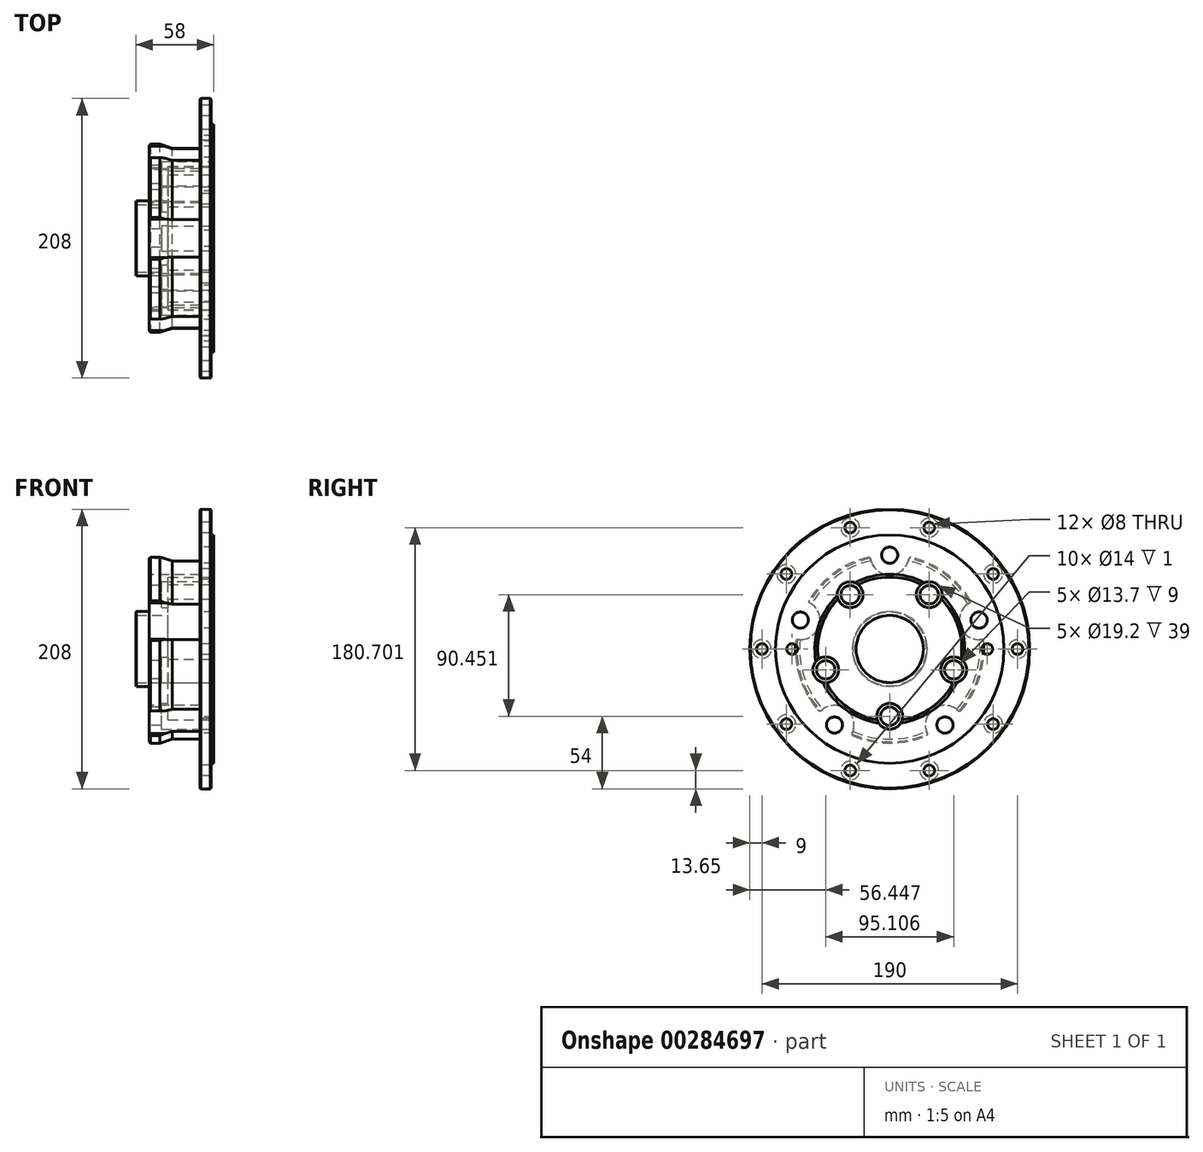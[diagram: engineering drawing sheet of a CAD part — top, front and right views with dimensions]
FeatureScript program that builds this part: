
annotation { "Feature Type Name" : "Feature", "Feature Type Description" : "" }
export const myFeature = defineFeature(function(context is Context, id is Id, definition is map)
    precondition{}
    {
        {
            var Q0;
            Q0=qCreatedBy(makeId("Front.planeOp"),FACE);
            var sketch = newSketch(context, id + "F0", { "sketchPlane" : qUnion([Q0])});
            skLineSegment(sketch, "E0", {"start": v(0, 0) * mm, "end": v(-58, 0) * mm});
            skLineSegment(sketch, "E1", {"start": v(0, 53.5) * mm, "end": v(0, 84.9) * mm});
            skLineSegment(sketch, "E2", {"start": v(0, 84.9) * mm, "end": v(-2.2, 84.9) * mm});
            skPoint(sketch, "E3", {"position": v(-2.2, 104) * mm});
            skLineSegment(sketch, "E4", {"start": v(-2.2, 84.9) * mm, "end": v(-2.2, 104) * mm});
            skLineSegment(sketch, "E5", {"start": v(-2.2, 104) * mm, "end": v(-10.2, 104) * mm});
            skPoint(sketch, "E6", {"position": v(-10.2, 67) * mm});
            skLineSegment(sketch, "E7", {"start": v(-10.2, 104) * mm, "end": v(-10.2, 67) * mm});
            skLineSegment(sketch, "E8", {"start": v(-10.2, 67) * mm, "end": v(-31, 67) * mm});
            skLineSegment(sketch, "E9", {"start": v(-31, 67) * mm, "end": v(-34, 67) * mm});
            skPoint(sketch, "E10", {"position": v(-48, 70) * mm});
            skLineSegment(sketch, "E11", {"start": v(-48, 70) * mm, "end": v(-48, 25) * mm});
            skPoint(sketch, "E12", {"position": v(-58, 27.85) * mm});
            skLineSegment(sketch, "E13", {"start": v(-58, 27.85) * mm, "end": v(-48, 27.85) * mm});
            skPoint(sketch, "E14", {"position": v(-58, 25) * mm});
            skLineSegment(sketch, "E15", {"start": v(-58, 25) * mm, "end": v(-48, 25) * mm});
            skLineSegment(sketch, "E16", {"start": v(-58, 27.85) * mm, "end": v(-58, 25) * mm});
            skPoint(sketch, "E17", {"position": v(0, 53.5) * mm});
            skLineSegment(sketch, "E18", {"start": v(0, 53.5) * mm, "end": v(-34, 53.5) * mm});
            skLineSegment(sketch, "E19", {"start": v(-34, 67) * mm, "end": v(-34, 0) * mm});
            skLineSegment(sketch, "E20", {"start": v(-34, 53.5) * mm, "end": v(-34, 25) * mm});
            skLineSegment(sketch, "E21", {"start": v(-48, 25) * mm, "end": v(-34, 25) * mm});
            skPoint(sketch, "E22.orphan", {"position": v(-34, 0) * mm});
            skPoint(sketch, "E23.orphan", {"position": v(-48, 0) * mm});
            skLineSegment(sketch, "E24", {"start": v(-48, 70) * mm, "end": v(-40, 70) * mm});
            skLineSegment(sketch, "E25", {"start": v(-40, 70) * mm, "end": v(-31, 67) * mm});
            skSolve(sketch);
        }
        {
            var Q0;
            Q0=qSketchRegion(id+"F0",true);
            var Q1;
            Q1=sQuery(id+"F0.wireOp",EDGE,"E0");
            revolve(context, id + "F1", {"entities" : qUnion([Q0]), "axis" : qUnion([Q1]), "revolveType" : RevolveType.FULL});
        }
        {
            var Q0;
            Q0=makeQuery(id+"F1.opRevolve","SWEPT_FACE",FACE,{"disambiguationData":[OSD([sQuery(id+"F0.wireOp",EDGE,"E11")])]});
            var sketch = newSketch(context, id + "F2", { "sketchPlane" : qUnion([Q0])});
            skPoint(sketch, "E26", {"position": v(0, 0) * mm});
            skCircle(sketch, "E27", {"center": v(0, 0) * mm, "radius": 69.85 * mm, "construction": true});
            skLineSegment(sketch, "E28", {"start": v(0, 0) * mm, "end": v(0, 69.85) * mm});
            skCircle(sketch, "E29", {"center": v(0, 69.85) * mm, "radius": 6 * mm});
            skCircle(sketch, "E30.1.0", {"center": v(-66.43, 21.58) * mm, "radius": 6 * mm});
            skCircle(sketch, "E30.2.0", {"center": v(-41.06, -56.5) * mm, "radius": 6 * mm});
            skCircle(sketch, "E30.3.0", {"center": v(41.06, -56.5) * mm, "radius": 6 * mm});
            skCircle(sketch, "E30.4.0", {"center": v(66.43, 21.58) * mm, "radius": 6 * mm});
            skSolve(sketch);
        }
        {
            var Q0;
            {var subQ0=sQuery(id+"F2.wireOp",EDGE,"9778c2bb-2c79-4bee-9a48-f8a60644cc8f.1.0");var subQ1=makeQuery(id+"F1.opRevolve","SWEPT_EDGE",EDGE,{"disambiguationData":[OSD([sQuery(id+"F0.wireOp",EDGE,"E11"),sQuery(id+"F0.wireOp",EDGE,"E24")])]});var subQ2=makeQuery(id+"F2.imprint","INTERSECT",VERTEX,{"disambiguationData":[OD(0.0)],"derivedFrom":[subQ1,subQ0]});Q0=makeQuery(id+"F2.imprint","IMPRINT",FACE,{"disambiguationData":[TD([[makeQuery(id+"F2.imprint","IMPRINT",EDGE,{"disambiguationData":[TD([[subQ2,1.0]])],"derivedFrom":subQ0}),1.0]])]});}
            var Q1;
            {var subQ0=sQuery(id+"F2.wireOp",EDGE,"9778c2bb-2c79-4bee-9a48-f8a60644cc8f.1.0");var subQ1=makeQuery(id+"F1.opRevolve","SWEPT_EDGE",EDGE,{"disambiguationData":[OSD([sQuery(id+"F0.wireOp",EDGE,"E11"),sQuery(id+"F0.wireOp",EDGE,"E24")])]});var subQ2=makeQuery(id+"F2.imprint","INTERSECT",VERTEX,{"disambiguationData":[OD(0.0)],"derivedFrom":[subQ1,subQ0]});Q1=makeQuery(id+"F2.imprint","IMPRINT",FACE,{"disambiguationData":[TD([[makeQuery(id+"F2.imprint","IMPRINT",EDGE,{"disambiguationData":[TD([[subQ2,-1.0]])],"derivedFrom":subQ0}),1.0]])]});}
            var Q2;
            {var subQ0=sQuery(id+"F2.wireOp",EDGE,"E29");var subQ1=makeQuery(id+"F1.opRevolve","SWEPT_EDGE",EDGE,{"disambiguationData":[OSD([sQuery(id+"F0.wireOp",EDGE,"E11"),sQuery(id+"F0.wireOp",EDGE,"E24")])]});var subQ2=makeQuery(id+"F2.imprint","INTERSECT",VERTEX,{"disambiguationData":[OD(0.0)],"derivedFrom":[subQ1,subQ0]});Q2=makeQuery(id+"F2.imprint","IMPRINT",FACE,{"disambiguationData":[TD([[makeQuery(id+"F2.imprint","IMPRINT",EDGE,{"disambiguationData":[TD([[subQ2,1.0]])],"derivedFrom":subQ0}),1.0]])]});}
            var Q3;
            {var subQ0=sQuery(id+"F2.wireOp",EDGE,"E29");var subQ1=makeQuery(id+"F2.imprint","IMPRINT",VERTEX,{"derivedFrom":subQ0});Q3=makeQuery(id+"F2.imprint","IMPRINT",FACE,{"disambiguationData":[TD([[makeQuery(id+"F2.imprint","IMPRINT",EDGE,{"disambiguationData":[TD([[subQ1,1.0]])],"derivedFrom":subQ0}),1.0]])]});}
            var Q4;
            {var subQ0=sQuery(id+"F2.wireOp",EDGE,"9778c2bb-2c79-4bee-9a48-f8a60644cc8f.4.0");var subQ1=makeQuery(id+"F1.opRevolve","SWEPT_EDGE",EDGE,{"disambiguationData":[OSD([sQuery(id+"F0.wireOp",EDGE,"E11"),sQuery(id+"F0.wireOp",EDGE,"E24")])]});var subQ2=makeQuery(id+"F2.imprint","INTERSECT",VERTEX,{"disambiguationData":[OD(0.0)],"derivedFrom":[subQ1,subQ0]});Q4=makeQuery(id+"F2.imprint","IMPRINT",FACE,{"disambiguationData":[TD([[makeQuery(id+"F2.imprint","IMPRINT",EDGE,{"disambiguationData":[TD([[subQ2,1.0]])],"derivedFrom":subQ0}),1.0]])]});}
            var Q5;
            {var subQ0=sQuery(id+"F2.wireOp",EDGE,"9778c2bb-2c79-4bee-9a48-f8a60644cc8f.4.0");var subQ1=makeQuery(id+"F1.opRevolve","SWEPT_EDGE",EDGE,{"disambiguationData":[OSD([sQuery(id+"F0.wireOp",EDGE,"E11"),sQuery(id+"F0.wireOp",EDGE,"E24")])]});var subQ2=makeQuery(id+"F2.imprint","INTERSECT",VERTEX,{"disambiguationData":[OD(0.0)],"derivedFrom":[subQ1,subQ0]});Q5=makeQuery(id+"F2.imprint","IMPRINT",FACE,{"disambiguationData":[TD([[makeQuery(id+"F2.imprint","IMPRINT",EDGE,{"disambiguationData":[TD([[subQ2,-1.0]])],"derivedFrom":subQ0}),1.0]])]});}
            var Q6;
            {var subQ0=sQuery(id+"F2.wireOp",EDGE,"9778c2bb-2c79-4bee-9a48-f8a60644cc8f.3.0");var subQ1=makeQuery(id+"F1.opRevolve","SWEPT_EDGE",EDGE,{"disambiguationData":[OSD([sQuery(id+"F0.wireOp",EDGE,"E11"),sQuery(id+"F0.wireOp",EDGE,"E24")])]});var subQ2=makeQuery(id+"F2.imprint","INTERSECT",VERTEX,{"disambiguationData":[OD(0.0)],"derivedFrom":[subQ1,subQ0]});Q6=makeQuery(id+"F2.imprint","IMPRINT",FACE,{"disambiguationData":[TD([[makeQuery(id+"F2.imprint","IMPRINT",EDGE,{"disambiguationData":[TD([[subQ2,1.0]])],"derivedFrom":subQ0}),1.0]])]});}
            var Q7;
            {var subQ0=sQuery(id+"F2.wireOp",EDGE,"9778c2bb-2c79-4bee-9a48-f8a60644cc8f.3.0");var subQ1=makeQuery(id+"F1.opRevolve","SWEPT_EDGE",EDGE,{"disambiguationData":[OSD([sQuery(id+"F0.wireOp",EDGE,"E11"),sQuery(id+"F0.wireOp",EDGE,"E24")])]});var subQ2=makeQuery(id+"F2.imprint","INTERSECT",VERTEX,{"disambiguationData":[OD(0.0)],"derivedFrom":[subQ1,subQ0]});Q7=makeQuery(id+"F2.imprint","IMPRINT",FACE,{"disambiguationData":[TD([[makeQuery(id+"F2.imprint","IMPRINT",EDGE,{"disambiguationData":[TD([[subQ2,-1.0]])],"derivedFrom":subQ0}),1.0]])]});}
            var Q8;
            {var subQ0=sQuery(id+"F2.wireOp",EDGE,"9778c2bb-2c79-4bee-9a48-f8a60644cc8f.2.0");var subQ1=makeQuery(id+"F1.opRevolve","SWEPT_EDGE",EDGE,{"disambiguationData":[OSD([sQuery(id+"F0.wireOp",EDGE,"E11"),sQuery(id+"F0.wireOp",EDGE,"E24")])]});var subQ2=makeQuery(id+"F2.imprint","INTERSECT",VERTEX,{"disambiguationData":[OD(0.0)],"derivedFrom":[subQ1,subQ0]});Q8=makeQuery(id+"F2.imprint","IMPRINT",FACE,{"disambiguationData":[TD([[makeQuery(id+"F2.imprint","IMPRINT",EDGE,{"disambiguationData":[TD([[subQ2,-1.0]])],"derivedFrom":subQ0}),1.0]])]});}
            var Q9;
            {var subQ0=sQuery(id+"F2.wireOp",EDGE,"9778c2bb-2c79-4bee-9a48-f8a60644cc8f.2.0");var subQ1=makeQuery(id+"F1.opRevolve","SWEPT_EDGE",EDGE,{"disambiguationData":[OSD([sQuery(id+"F0.wireOp",EDGE,"E11"),sQuery(id+"F0.wireOp",EDGE,"E24")])]});var subQ2=makeQuery(id+"F2.imprint","INTERSECT",VERTEX,{"disambiguationData":[OD(0.0)],"derivedFrom":[subQ1,subQ0]});Q9=makeQuery(id+"F2.imprint","IMPRINT",FACE,{"disambiguationData":[TD([[makeQuery(id+"F2.imprint","IMPRINT",EDGE,{"disambiguationData":[TD([[subQ2,1.0]])],"derivedFrom":subQ0}),1.0]])]});}
            var Q10;
            {var subQ0=sQuery(id+"F2.wireOp",EDGE,"E30.1.0");var subQ1=makeQuery(id+"F1.opRevolve","SWEPT_EDGE",EDGE,{"disambiguationData":[OSD([sQuery(id+"F0.wireOp",EDGE,"E11"),sQuery(id+"F0.wireOp",EDGE,"E24")])]});var subQ2=makeQuery(id+"F2.imprint","INTERSECT",VERTEX,{"disambiguationData":[OD(0.0)],"derivedFrom":[subQ1,subQ0]});Q10=makeQuery(id+"F2.imprint","IMPRINT",FACE,{"disambiguationData":[TD([[makeQuery(id+"F2.imprint","IMPRINT",EDGE,{"disambiguationData":[TD([[subQ2,-1.0]])],"derivedFrom":subQ0}),1.0]])]});}
            var Q11;
            {var subQ0=sQuery(id+"F2.wireOp",EDGE,"E30.1.0");var subQ1=makeQuery(id+"F1.opRevolve","SWEPT_EDGE",EDGE,{"disambiguationData":[OSD([sQuery(id+"F0.wireOp",EDGE,"E11"),sQuery(id+"F0.wireOp",EDGE,"E24")])]});var subQ2=makeQuery(id+"F2.imprint","INTERSECT",VERTEX,{"disambiguationData":[OD(0.0)],"derivedFrom":[subQ1,subQ0]});Q11=makeQuery(id+"F2.imprint","IMPRINT",FACE,{"disambiguationData":[TD([[makeQuery(id+"F2.imprint","IMPRINT",EDGE,{"disambiguationData":[TD([[subQ2,1.0]])],"derivedFrom":subQ0}),1.0]])]});}
            var Q12;
            {var subQ0=sQuery(id+"F2.wireOp",EDGE,"E30.2.0");var subQ1=makeQuery(id+"F1.opRevolve","SWEPT_EDGE",EDGE,{"disambiguationData":[OSD([sQuery(id+"F0.wireOp",EDGE,"E11"),sQuery(id+"F0.wireOp",EDGE,"E24")])]});var subQ2=makeQuery(id+"F2.imprint","INTERSECT",VERTEX,{"disambiguationData":[OD(0.0)],"derivedFrom":[subQ1,subQ0]});Q12=makeQuery(id+"F2.imprint","IMPRINT",FACE,{"disambiguationData":[TD([[makeQuery(id+"F2.imprint","IMPRINT",EDGE,{"disambiguationData":[TD([[subQ2,-1.0]])],"derivedFrom":subQ0}),1.0]])]});}
            var Q13;
            {var subQ0=sQuery(id+"F2.wireOp",EDGE,"E30.2.0");var subQ1=makeQuery(id+"F1.opRevolve","SWEPT_EDGE",EDGE,{"disambiguationData":[OSD([sQuery(id+"F0.wireOp",EDGE,"E11"),sQuery(id+"F0.wireOp",EDGE,"E24")])]});var subQ2=makeQuery(id+"F2.imprint","INTERSECT",VERTEX,{"disambiguationData":[OD(0.0)],"derivedFrom":[subQ1,subQ0]});Q13=makeQuery(id+"F2.imprint","IMPRINT",FACE,{"disambiguationData":[TD([[makeQuery(id+"F2.imprint","IMPRINT",EDGE,{"disambiguationData":[TD([[subQ2,1.0]])],"derivedFrom":subQ0}),1.0]])]});}
            var Q14;
            {var subQ0=sQuery(id+"F2.wireOp",EDGE,"E30.3.0");var subQ1=makeQuery(id+"F1.opRevolve","SWEPT_EDGE",EDGE,{"disambiguationData":[OSD([sQuery(id+"F0.wireOp",EDGE,"E11"),sQuery(id+"F0.wireOp",EDGE,"E24")])]});var subQ2=makeQuery(id+"F2.imprint","INTERSECT",VERTEX,{"disambiguationData":[OD(0.0)],"derivedFrom":[subQ1,subQ0]});Q14=makeQuery(id+"F2.imprint","IMPRINT",FACE,{"disambiguationData":[TD([[makeQuery(id+"F2.imprint","IMPRINT",EDGE,{"disambiguationData":[TD([[subQ2,1.0]])],"derivedFrom":subQ0}),1.0]])]});}
            var Q15;
            {var subQ0=sQuery(id+"F2.wireOp",EDGE,"E30.3.0");var subQ1=makeQuery(id+"F1.opRevolve","SWEPT_EDGE",EDGE,{"disambiguationData":[OSD([sQuery(id+"F0.wireOp",EDGE,"E11"),sQuery(id+"F0.wireOp",EDGE,"E24")])]});var subQ2=makeQuery(id+"F2.imprint","INTERSECT",VERTEX,{"disambiguationData":[OD(0.0)],"derivedFrom":[subQ1,subQ0]});Q15=makeQuery(id+"F2.imprint","IMPRINT",FACE,{"disambiguationData":[TD([[makeQuery(id+"F2.imprint","IMPRINT",EDGE,{"disambiguationData":[TD([[subQ2,-1.0]])],"derivedFrom":subQ0}),1.0]])]});}
            var Q16;
            {var subQ0=sQuery(id+"F2.wireOp",EDGE,"E30.4.0");var subQ1=makeQuery(id+"F1.opRevolve","SWEPT_EDGE",EDGE,{"disambiguationData":[OSD([sQuery(id+"F0.wireOp",EDGE,"E11"),sQuery(id+"F0.wireOp",EDGE,"E24")])]});var subQ2=makeQuery(id+"F2.imprint","INTERSECT",VERTEX,{"disambiguationData":[OD(0.0)],"derivedFrom":[subQ1,subQ0]});Q16=makeQuery(id+"F2.imprint","IMPRINT",FACE,{"disambiguationData":[TD([[makeQuery(id+"F2.imprint","IMPRINT",EDGE,{"disambiguationData":[TD([[subQ2,1.0]])],"derivedFrom":subQ0}),1.0]])]});}
            var Q17;
            {var subQ0=sQuery(id+"F2.wireOp",EDGE,"E30.4.0");var subQ1=makeQuery(id+"F1.opRevolve","SWEPT_EDGE",EDGE,{"disambiguationData":[OSD([sQuery(id+"F0.wireOp",EDGE,"E11"),sQuery(id+"F0.wireOp",EDGE,"E24")])]});var subQ2=makeQuery(id+"F2.imprint","INTERSECT",VERTEX,{"disambiguationData":[OD(0.0)],"derivedFrom":[subQ1,subQ0]});Q17=makeQuery(id+"F2.imprint","IMPRINT",FACE,{"disambiguationData":[TD([[makeQuery(id+"F2.imprint","IMPRINT",EDGE,{"disambiguationData":[TD([[subQ2,-1.0]])],"derivedFrom":subQ0}),1.0]])]});}
            extrude(context, id + "F3", {"entities" : qUnion([Q0, Q1, Q2, Q3, Q4, Q5, Q6, Q7, Q8, Q9, Q10, Q11, Q12, Q13, Q14, Q15, Q16, Q17]), "operationType" : NewBodyOperationType.REMOVE, "oppositeDirection" : true, "depth" : 48 * mm});
        }
        {
            var Q0;
            Q0=makeQuery(id+"F1.opRevolve","SWEPT_FACE",FACE,{"disambiguationData":[OSD([sQuery(id+"F0.wireOp",EDGE,"E11")])]});
            var sketch = newSketch(context, id + "F4", { "sketchPlane" : qUnion([Q0])});
            skCircle(sketch, "E31.0", {"center": v(0, 0) * mm, "radius": 25 * mm, "construction": true});
            skCircle(sketch, "E32", {"center": v(0, 0) * mm, "radius": 69.7 * mm, "construction": true});
            skPoint(sketch, "E33", {"position": v(0, 69.7) * mm});
            skCircle(sketch, "E34", {"center": v(0, 69.7) * mm, "radius": 14.5 * mm});
            skCircle(sketch, "E35.1.0", {"center": v(-66.29, 21.54) * mm, "radius": 14.5 * mm});
            skCircle(sketch, "E35.2.0", {"center": v(-40.97, -56.39) * mm, "radius": 14.5 * mm});
            skCircle(sketch, "E35.3.0", {"center": v(40.97, -56.39) * mm, "radius": 14.5 * mm});
            skCircle(sketch, "E35.4.0", {"center": v(66.29, 21.54) * mm, "radius": 14.5 * mm});
            skSolve(sketch);
        }
        {
            var Q0;
            Q0=qSketchRegion(id+"F4",true);
            extrude(context, id + "F5", {"entities" : qUnion([Q0]), "operationType" : NewBodyOperationType.REMOVE, "oppositeDirection" : true, "depth" : 37.8 * mm});
        }
        {
            var Q0;
            Q0=makeQuery(id+"F1.opRevolve","SWEPT_FACE",FACE,{"disambiguationData":[OSD([sQuery(id+"F0.wireOp",EDGE,"E11")])]});
            var sketch = newSketch(context, id + "F6", { "sketchPlane" : qUnion([Q0])});
            skCircle(sketch, "E36", {"center": v(0, 0) * mm, "radius": 50 * mm, "construction": true});
            skLineSegment(sketch, "E37", {"start": v(0, 0) * mm, "end": v(-29.39, 40.45) * mm});
            skCircle(sketch, "E38", {"center": v(-29.39, 40.45) * mm, "radius": 6.85 * mm});
            skCircle(sketch, "E39.1.0", {"center": v(-47.55, -15.45) * mm, "radius": 6.85 * mm});
            skCircle(sketch, "E39.2.0", {"center": v(0, -50) * mm, "radius": 6.85 * mm});
            skCircle(sketch, "E39.3.0", {"center": v(47.55, -15.45) * mm, "radius": 6.85 * mm});
            skCircle(sketch, "E39.4.0", {"center": v(29.39, 40.45) * mm, "radius": 6.85 * mm});
            skSolve(sketch);
        }
        {
            var Q0;
            Q0=qSketchRegion(id+"F6",true);
            extrude(context, id + "F7", {"entities" : qUnion([Q0]), "operationType" : NewBodyOperationType.REMOVE, "oppositeDirection" : true, "depth" : 14 * mm});
        }
        {
            var Q0;
            Q0=makeQuery(id+"F1.opRevolve","SWEPT_FACE",FACE,{"disambiguationData":[OSD([sQuery(id+"F0.wireOp",EDGE,"E1")])]});
            var sketch = newSketch(context, id + "F8", { "sketchPlane" : qUnion([Q0])});
            skCircle(sketch, "E40", {"center": v(0, 0) * mm, "radius": 50 * mm, "construction": true});
            skArc(sketch, "E41.0", {"start": v(-26.32, 46.58) * mm, "mid": v(-25.36, 34.9) * mm, "end": v(-36.16, 39.43) * mm, "construction": true});
            skCircle(sketch, "E42", {"center": v(-29.39, 40.45) * mm, "radius": 9.6 * mm});
            skCircle(sketch, "E43.1.0", {"center": v(-47.55, -15.45) * mm, "radius": 9.6 * mm});
            skCircle(sketch, "E43.2.0", {"center": v(0, -50) * mm, "radius": 9.6 * mm});
            skCircle(sketch, "E43.3.0", {"center": v(47.55, -15.45) * mm, "radius": 9.6 * mm});
            skCircle(sketch, "E43.4.0", {"center": v(29.39, 40.45) * mm, "radius": 9.6 * mm});
            skSolve(sketch);
        }
        {
            var Q0;
            Q0=qSketchRegion(id+"F8",true);
            extrude(context, id + "F9", {"entities" : qUnion([Q0]), "operationType" : NewBodyOperationType.REMOVE, "oppositeDirection" : true, "depth" : 39 * mm});
        }
        {
            var Q0;
            Q0=makeQuery(id+"F5.boolean.opBoolean","MERGE",FACE,{"derivedFrom":[makeQuery(id+"F1.opRevolve","SWEPT_FACE",FACE,{"disambiguationData":[OSD([sQuery(id+"F0.wireOp",EDGE,"E7")])]}),makeQuery(id+"F5.opExtrude","CAP_FACE",FACE,{"disambiguationData":[OSD([sQuery(id+"F4.wireOp",EDGE,"E34")])],"isStart":false}),makeQuery(id+"F5.opExtrude","CAP_FACE",FACE,{"disambiguationData":[OSD([sQuery(id+"F4.wireOp",EDGE,"E35.1.0")])],"isStart":false}),makeQuery(id+"F5.opExtrude","CAP_FACE",FACE,{"disambiguationData":[OSD([sQuery(id+"F4.wireOp",EDGE,"E35.2.0")])],"isStart":false}),makeQuery(id+"F5.opExtrude","CAP_FACE",FACE,{"disambiguationData":[OSD([sQuery(id+"F4.wireOp",EDGE,"E35.3.0")])],"isStart":false}),makeQuery(id+"F5.opExtrude","CAP_FACE",FACE,{"disambiguationData":[OSD([sQuery(id+"F4.wireOp",EDGE,"E35.4.0")])],"isStart":false})]});
            var sketch = newSketch(context, id + "F10", { "sketchPlane" : qUnion([Q0])});
            skLineSegment(sketch, "E44", {"start": v(0, 0) * mm, "end": v(-29.36, 90.35) * mm});
            skCircle(sketch, "E45", {"center": v(0, 0) * mm, "radius": 95 * mm, "construction": true});
            skCircle(sketch, "E46", {"center": v(-29.36, 90.35) * mm, "radius": 4 * mm});
            skCircle(sketch, "E47.1.0", {"center": v(-76.86, 55.84) * mm, "radius": 4 * mm});
            skCircle(sketch, "E47.2.0", {"center": v(-95, 0) * mm, "radius": 4 * mm});
            skCircle(sketch, "E47.3.0", {"center": v(-76.86, -55.84) * mm, "radius": 4 * mm});
            skCircle(sketch, "E47.4.0", {"center": v(-29.36, -90.35) * mm, "radius": 4 * mm});
            skCircle(sketch, "E47.5.0", {"center": v(29.36, -90.35) * mm, "radius": 4 * mm});
            skCircle(sketch, "E47.6.0", {"center": v(76.86, -55.84) * mm, "radius": 4 * mm});
            skCircle(sketch, "E47.7.0", {"center": v(95, 0) * mm, "radius": 4 * mm});
            skCircle(sketch, "E47.8.0", {"center": v(76.86, 55.84) * mm, "radius": 4 * mm});
            skCircle(sketch, "E47.9.0", {"center": v(29.36, 90.35) * mm, "radius": 4 * mm});
            skSolve(sketch);
        }
        {
            var Q0;
            Q0=qSketchRegion(id+"F10",true);
            extrude(context, id + "F11", {"entities" : qUnion([Q0]), "operationType" : NewBodyOperationType.REMOVE, "oppositeDirection" : true, "depth" : 8 * mm});
        }
        {
            var Q0;
            Q0=makeQuery(id+"F5.boolean.opBoolean","MERGE",FACE,{"derivedFrom":[makeQuery(id+"F1.opRevolve","SWEPT_FACE",FACE,{"disambiguationData":[OSD([sQuery(id+"F0.wireOp",EDGE,"E7")])]}),makeQuery(id+"F5.opExtrude","CAP_FACE",FACE,{"disambiguationData":[OSD([sQuery(id+"F4.wireOp",EDGE,"E34")])],"isStart":false}),makeQuery(id+"F5.opExtrude","CAP_FACE",FACE,{"disambiguationData":[OSD([sQuery(id+"F4.wireOp",EDGE,"E35.1.0")])],"isStart":false}),makeQuery(id+"F5.opExtrude","CAP_FACE",FACE,{"disambiguationData":[OSD([sQuery(id+"F4.wireOp",EDGE,"E35.2.0")])],"isStart":false}),makeQuery(id+"F5.opExtrude","CAP_FACE",FACE,{"disambiguationData":[OSD([sQuery(id+"F4.wireOp",EDGE,"E35.3.0")])],"isStart":false}),makeQuery(id+"F5.opExtrude","CAP_FACE",FACE,{"disambiguationData":[OSD([sQuery(id+"F4.wireOp",EDGE,"E35.4.0")])],"isStart":false})]});
            var sketch = newSketch(context, id + "F12", { "sketchPlane" : qUnion([Q0])});
            skCircle(sketch, "E48", {"center": v(0, 0) * mm, "radius": 95 * mm, "construction": true});
            skCircle(sketch, "E49.0", {"center": v(-29.36, 90.35) * mm, "radius": 4 * mm, "construction": true});
            skCircle(sketch, "E50", {"center": v(-29.36, 90.35) * mm, "radius": 7 * mm});
            skCircle(sketch, "E51.1.0", {"center": v(-76.86, 55.84) * mm, "radius": 7 * mm});
            skCircle(sketch, "E51.2.0", {"center": v(-95, 0) * mm, "radius": 7 * mm});
            skCircle(sketch, "E51.3.0", {"center": v(-76.86, -55.84) * mm, "radius": 7 * mm});
            skCircle(sketch, "E51.4.0", {"center": v(-29.36, -90.35) * mm, "radius": 7 * mm});
            skCircle(sketch, "E51.5.0", {"center": v(29.36, -90.35) * mm, "radius": 7 * mm});
            skCircle(sketch, "E51.6.0", {"center": v(76.86, -55.84) * mm, "radius": 7 * mm});
            skCircle(sketch, "E51.7.0", {"center": v(95, 0) * mm, "radius": 7 * mm});
            skCircle(sketch, "E51.8.0", {"center": v(76.86, 55.84) * mm, "radius": 7 * mm});
            skCircle(sketch, "E51.9.0", {"center": v(29.36, 90.35) * mm, "radius": 7 * mm});
            skSolve(sketch);
        }
        {
            var Q0;
            Q0=qSketchRegion(id+"F12",true);
            extrude(context, id + "F13", {"entities" : qUnion([Q0]), "operationType" : NewBodyOperationType.REMOVE, "oppositeDirection" : true, "depth" : 1 * mm});
        }
        {
            var Q0;
            {var subQ0=sQuery(id+"F0.wireOp",EDGE,"E1");var subQ1=sQuery(id+"F0.wireOp",EDGE,"E18");Q0=makeQuery(id+"F9.boolean.opBoolean","SPLIT",EDGE,{"disambiguationData":[TD([makeQuery(id+"F1.opRevolve","SWEPT_FACE",FACE,{"disambiguationData":[OSD([subQ0])]}),makeQuery(id+"F1.opRevolve","SWEPT_FACE",FACE,{"disambiguationData":[OSD([subQ1])]}),makeQuery(id+"F9.opExtrude","SWEPT_FACE",FACE,{"disambiguationData":[OSD([sQuery(id+"F8.wireOp",EDGE,"E42")])]}),makeQuery(id+"F9.opExtrude","SWEPT_FACE",FACE,{"disambiguationData":[OSD([sQuery(id+"F8.wireOp",EDGE,"E43.4.0")])]})])],"derivedFrom":makeQuery(id+"F1.opRevolve","SWEPT_EDGE",EDGE,{"disambiguationData":[OSD([subQ0,subQ1])]})});}
            var Q1;
            {var subQ0=sQuery(id+"F0.wireOp",EDGE,"E1");var subQ1=sQuery(id+"F0.wireOp",EDGE,"E18");Q1=makeQuery(id+"F9.boolean.opBoolean","SPLIT",EDGE,{"disambiguationData":[TD([makeQuery(id+"F1.opRevolve","SWEPT_FACE",FACE,{"disambiguationData":[OSD([subQ0])]}),makeQuery(id+"F1.opRevolve","SWEPT_FACE",FACE,{"disambiguationData":[OSD([subQ1])]}),makeQuery(id+"F9.opExtrude","SWEPT_FACE",FACE,{"disambiguationData":[OSD([sQuery(id+"F8.wireOp",EDGE,"E43.3.0")])]}),makeQuery(id+"F9.opExtrude","SWEPT_FACE",FACE,{"disambiguationData":[OSD([sQuery(id+"F8.wireOp",EDGE,"E43.4.0")])]})])],"derivedFrom":makeQuery(id+"F1.opRevolve","SWEPT_EDGE",EDGE,{"disambiguationData":[OSD([subQ0,subQ1])]})});}
            var Q2;
            {var subQ0=sQuery(id+"F0.wireOp",EDGE,"E1");var subQ1=sQuery(id+"F0.wireOp",EDGE,"E18");Q2=makeQuery(id+"F9.boolean.opBoolean","SPLIT",EDGE,{"disambiguationData":[TD([makeQuery(id+"F1.opRevolve","SWEPT_FACE",FACE,{"disambiguationData":[OSD([subQ0])]}),makeQuery(id+"F1.opRevolve","SWEPT_FACE",FACE,{"disambiguationData":[OSD([subQ1])]}),makeQuery(id+"F9.opExtrude","SWEPT_FACE",FACE,{"disambiguationData":[OSD([sQuery(id+"F8.wireOp",EDGE,"E43.2.0")])]}),makeQuery(id+"F9.opExtrude","SWEPT_FACE",FACE,{"disambiguationData":[OSD([sQuery(id+"F8.wireOp",EDGE,"E43.3.0")])]})])],"derivedFrom":makeQuery(id+"F1.opRevolve","SWEPT_EDGE",EDGE,{"disambiguationData":[OSD([subQ0,subQ1])]})});}
            var Q3;
            {var subQ0=sQuery(id+"F0.wireOp",EDGE,"E1");var subQ1=sQuery(id+"F0.wireOp",EDGE,"E18");Q3=makeQuery(id+"F9.boolean.opBoolean","SPLIT",EDGE,{"disambiguationData":[TD([makeQuery(id+"F1.opRevolve","SWEPT_FACE",FACE,{"disambiguationData":[OSD([subQ0])]}),makeQuery(id+"F1.opRevolve","SWEPT_FACE",FACE,{"disambiguationData":[OSD([subQ1])]}),makeQuery(id+"F9.opExtrude","SWEPT_FACE",FACE,{"disambiguationData":[OSD([sQuery(id+"F8.wireOp",EDGE,"E43.1.0")])]}),makeQuery(id+"F9.opExtrude","SWEPT_FACE",FACE,{"disambiguationData":[OSD([sQuery(id+"F8.wireOp",EDGE,"E43.2.0")])]})])],"derivedFrom":makeQuery(id+"F1.opRevolve","SWEPT_EDGE",EDGE,{"disambiguationData":[OSD([subQ0,subQ1])]})});}
            var Q4;
            {var subQ0=sQuery(id+"F0.wireOp",EDGE,"E1");var subQ1=sQuery(id+"F0.wireOp",EDGE,"E18");Q4=makeQuery(id+"F9.boolean.opBoolean","SPLIT",EDGE,{"disambiguationData":[TD([makeQuery(id+"F1.opRevolve","SWEPT_FACE",FACE,{"disambiguationData":[OSD([subQ0])]}),makeQuery(id+"F1.opRevolve","SWEPT_FACE",FACE,{"disambiguationData":[OSD([subQ1])]}),makeQuery(id+"F9.opExtrude","SWEPT_FACE",FACE,{"disambiguationData":[OSD([sQuery(id+"F8.wireOp",EDGE,"E42")])]}),makeQuery(id+"F9.opExtrude","SWEPT_FACE",FACE,{"disambiguationData":[OSD([sQuery(id+"F8.wireOp",EDGE,"E43.1.0")])]})])],"derivedFrom":makeQuery(id+"F1.opRevolve","SWEPT_EDGE",EDGE,{"disambiguationData":[OSD([subQ0,subQ1])]})});}
            chamfer(context, id + "F14", {"entities" : qUnion([Q0, Q1, Q2, Q3, Q4]), "width" : 2.2 * mm, "tangentPropagation" : true});
        }
        {
            var Q0;
            {var subQ0=sQuery(id+"F0.wireOp",EDGE,"E11");var subQ1=sQuery(id+"F0.wireOp",EDGE,"E24");Q0=makeQuery(id+"F3.boolean.opBoolean","SPLIT",EDGE,{"disambiguationData":[TD([makeQuery(id+"F1.opRevolve","SWEPT_FACE",FACE,{"disambiguationData":[OSD([subQ0])]}),makeQuery(id+"F1.opRevolve","SWEPT_FACE",FACE,{"disambiguationData":[OSD([subQ1])]}),makeQuery(id+"F3.opExtrude","SWEPT_FACE",FACE,{"disambiguationData":[OSD([sQuery(id+"F2.wireOp",EDGE,"isoNOGXv-9rzR-vXjO-d8jj-fEhT8795Os4k")])]}),makeQuery(id+"F3.opExtrude","SWEPT_FACE",FACE,{"disambiguationData":[OSD([sQuery(id+"F2.wireOp",EDGE,"ed49934d-06d9-406b-9f25-b05f826b0471.4.0")])]})])],"derivedFrom":makeQuery(id+"F1.opRevolve","SWEPT_EDGE",EDGE,{"disambiguationData":[OSD([subQ0,subQ1])]})});}
            var Q1;
            Q1=makeQuery(id+"F5.boolean.opBoolean","COPY",EDGE,{"derivedFrom":makeQuery(id+"F5.opExtrude","CAP_EDGE",EDGE,{"disambiguationData":[OSD([sQuery(id+"F4.wireOp",EDGE,"E35.4.0")])],"isStart":true})});
            var Q2;
            {var subQ0=sQuery(id+"F0.wireOp",EDGE,"E11");var subQ1=sQuery(id+"F0.wireOp",EDGE,"E24");Q2=makeQuery(id+"F3.boolean.opBoolean","SPLIT",EDGE,{"disambiguationData":[TD([makeQuery(id+"F1.opRevolve","SWEPT_FACE",FACE,{"disambiguationData":[OSD([subQ0])]}),makeQuery(id+"F1.opRevolve","SWEPT_FACE",FACE,{"disambiguationData":[OSD([subQ1])]}),makeQuery(id+"F3.opExtrude","SWEPT_FACE",FACE,{"disambiguationData":[OSD([sQuery(id+"F2.wireOp",EDGE,"ed49934d-06d9-406b-9f25-b05f826b0471.3.0")])]}),makeQuery(id+"F3.opExtrude","SWEPT_FACE",FACE,{"disambiguationData":[OSD([sQuery(id+"F2.wireOp",EDGE,"ed49934d-06d9-406b-9f25-b05f826b0471.4.0")])]})])],"derivedFrom":makeQuery(id+"F1.opRevolve","SWEPT_EDGE",EDGE,{"disambiguationData":[OSD([subQ0,subQ1])]})});}
            var Q3;
            Q3=makeQuery(id+"F5.boolean.opBoolean","COPY",EDGE,{"derivedFrom":makeQuery(id+"F5.opExtrude","CAP_EDGE",EDGE,{"disambiguationData":[OSD([sQuery(id+"F4.wireOp",EDGE,"E35.3.0")])],"isStart":true})});
            var Q4;
            {var subQ0=sQuery(id+"F0.wireOp",EDGE,"E11");var subQ1=sQuery(id+"F0.wireOp",EDGE,"E24");Q4=makeQuery(id+"F3.boolean.opBoolean","SPLIT",EDGE,{"disambiguationData":[TD([makeQuery(id+"F1.opRevolve","SWEPT_FACE",FACE,{"disambiguationData":[OSD([subQ0])]}),makeQuery(id+"F1.opRevolve","SWEPT_FACE",FACE,{"disambiguationData":[OSD([subQ1])]}),makeQuery(id+"F3.opExtrude","SWEPT_FACE",FACE,{"disambiguationData":[OSD([sQuery(id+"F2.wireOp",EDGE,"ed49934d-06d9-406b-9f25-b05f826b0471.2.0")])]}),makeQuery(id+"F3.opExtrude","SWEPT_FACE",FACE,{"disambiguationData":[OSD([sQuery(id+"F2.wireOp",EDGE,"ed49934d-06d9-406b-9f25-b05f826b0471.3.0")])]})])],"derivedFrom":makeQuery(id+"F1.opRevolve","SWEPT_EDGE",EDGE,{"disambiguationData":[OSD([subQ0,subQ1])]})});}
            var Q5;
            Q5=makeQuery(id+"F5.boolean.opBoolean","COPY",EDGE,{"derivedFrom":makeQuery(id+"F5.opExtrude","CAP_EDGE",EDGE,{"disambiguationData":[OSD([sQuery(id+"F4.wireOp",EDGE,"E35.2.0")])],"isStart":true})});
            var Q6;
            {var subQ0=sQuery(id+"F0.wireOp",EDGE,"E11");var subQ1=sQuery(id+"F0.wireOp",EDGE,"E24");Q6=makeQuery(id+"F3.boolean.opBoolean","SPLIT",EDGE,{"disambiguationData":[TD([makeQuery(id+"F1.opRevolve","SWEPT_FACE",FACE,{"disambiguationData":[OSD([subQ0])]}),makeQuery(id+"F1.opRevolve","SWEPT_FACE",FACE,{"disambiguationData":[OSD([subQ1])]}),makeQuery(id+"F3.opExtrude","SWEPT_FACE",FACE,{"disambiguationData":[OSD([sQuery(id+"F2.wireOp",EDGE,"ed49934d-06d9-406b-9f25-b05f826b0471.1.0")])]}),makeQuery(id+"F3.opExtrude","SWEPT_FACE",FACE,{"disambiguationData":[OSD([sQuery(id+"F2.wireOp",EDGE,"ed49934d-06d9-406b-9f25-b05f826b0471.2.0")])]})])],"derivedFrom":makeQuery(id+"F1.opRevolve","SWEPT_EDGE",EDGE,{"disambiguationData":[OSD([subQ0,subQ1])]})});}
            var Q7;
            Q7=makeQuery(id+"F5.boolean.opBoolean","COPY",EDGE,{"derivedFrom":makeQuery(id+"F5.opExtrude","CAP_EDGE",EDGE,{"disambiguationData":[OSD([sQuery(id+"F4.wireOp",EDGE,"E35.1.0")])],"isStart":true})});
            var Q8;
            {var subQ0=sQuery(id+"F0.wireOp",EDGE,"E11");var subQ1=sQuery(id+"F0.wireOp",EDGE,"E24");Q8=makeQuery(id+"F3.boolean.opBoolean","SPLIT",EDGE,{"disambiguationData":[TD([makeQuery(id+"F1.opRevolve","SWEPT_FACE",FACE,{"disambiguationData":[OSD([subQ0])]}),makeQuery(id+"F1.opRevolve","SWEPT_FACE",FACE,{"disambiguationData":[OSD([subQ1])]}),makeQuery(id+"F3.opExtrude","SWEPT_FACE",FACE,{"disambiguationData":[OSD([sQuery(id+"F2.wireOp",EDGE,"isoNOGXv-9rzR-vXjO-d8jj-fEhT8795Os4k")])]}),makeQuery(id+"F3.opExtrude","SWEPT_FACE",FACE,{"disambiguationData":[OSD([sQuery(id+"F2.wireOp",EDGE,"ed49934d-06d9-406b-9f25-b05f826b0471.1.0")])]})])],"derivedFrom":makeQuery(id+"F1.opRevolve","SWEPT_EDGE",EDGE,{"disambiguationData":[OSD([subQ0,subQ1])]})});}
            var Q9;
            Q9=makeQuery(id+"F5.boolean.opBoolean","COPY",EDGE,{"derivedFrom":makeQuery(id+"F5.opExtrude","CAP_EDGE",EDGE,{"disambiguationData":[OSD([sQuery(id+"F4.wireOp",EDGE,"E34")])],"isStart":true})});
            var Q10;
            Q10=makeQuery(id+"F5.boolean.opBoolean","INTERSECT",EDGE,{"derivedFrom":[makeQuery(id+"F3.boolean.opBoolean","SPLIT",FACE,{"disambiguationData":[TD([makeQuery(id+"F1.opRevolve","SWEPT_FACE",FACE,{"disambiguationData":[OSD([sQuery(id+"F0.wireOp",EDGE,"E11")])]}),makeQuery(id+"F1.opRevolve","SWEPT_FACE",FACE,{"disambiguationData":[OSD([sQuery(id+"F0.wireOp",EDGE,"E25")])]}),makeQuery(id+"F3.opExtrude","SWEPT_FACE",FACE,{"disambiguationData":[OSD([sQuery(id+"F2.wireOp",EDGE,"isoNOGXv-9rzR-vXjO-d8jj-fEhT8795Os4k")])]}),makeQuery(id+"F3.opExtrude","SWEPT_FACE",FACE,{"disambiguationData":[OSD([sQuery(id+"F2.wireOp",EDGE,"ed49934d-06d9-406b-9f25-b05f826b0471.4.0")])]})])],"derivedFrom":makeQuery(id+"F1.opRevolve","SWEPT_FACE",FACE,{"disambiguationData":[OSD([sQuery(id+"F0.wireOp",EDGE,"E24")])]})}),makeQuery(id+"F5.opExtrude","SWEPT_FACE",FACE,{"disambiguationData":[OSD([sQuery(id+"F4.wireOp",EDGE,"E34")])]})]});
            var Q11;
            Q11=makeQuery(id+"F5.boolean.opBoolean","INTERSECT",EDGE,{"derivedFrom":[makeQuery(id+"F3.boolean.opBoolean","SPLIT",FACE,{"disambiguationData":[TD([makeQuery(id+"F1.opRevolve","SWEPT_FACE",FACE,{"disambiguationData":[OSD([sQuery(id+"F0.wireOp",EDGE,"E11")])]}),makeQuery(id+"F1.opRevolve","SWEPT_FACE",FACE,{"disambiguationData":[OSD([sQuery(id+"F0.wireOp",EDGE,"E25")])]}),makeQuery(id+"F3.opExtrude","SWEPT_FACE",FACE,{"disambiguationData":[OSD([sQuery(id+"F2.wireOp",EDGE,"isoNOGXv-9rzR-vXjO-d8jj-fEhT8795Os4k")])]}),makeQuery(id+"F3.opExtrude","SWEPT_FACE",FACE,{"disambiguationData":[OSD([sQuery(id+"F2.wireOp",EDGE,"ed49934d-06d9-406b-9f25-b05f826b0471.1.0")])]})])],"derivedFrom":makeQuery(id+"F1.opRevolve","SWEPT_FACE",FACE,{"disambiguationData":[OSD([sQuery(id+"F0.wireOp",EDGE,"E24")])]})}),makeQuery(id+"F5.opExtrude","SWEPT_FACE",FACE,{"disambiguationData":[OSD([sQuery(id+"F4.wireOp",EDGE,"E34")])]})]});
            var Q12;
            Q12=makeQuery(id+"F5.boolean.opBoolean","INTERSECT",EDGE,{"derivedFrom":[makeQuery(id+"F3.boolean.opBoolean","SPLIT",FACE,{"disambiguationData":[TD([makeQuery(id+"F1.opRevolve","SWEPT_FACE",FACE,{"disambiguationData":[OSD([sQuery(id+"F0.wireOp",EDGE,"E11")])]}),makeQuery(id+"F1.opRevolve","SWEPT_FACE",FACE,{"disambiguationData":[OSD([sQuery(id+"F0.wireOp",EDGE,"E25")])]}),makeQuery(id+"F3.opExtrude","SWEPT_FACE",FACE,{"disambiguationData":[OSD([sQuery(id+"F2.wireOp",EDGE,"isoNOGXv-9rzR-vXjO-d8jj-fEhT8795Os4k")])]}),makeQuery(id+"F3.opExtrude","SWEPT_FACE",FACE,{"disambiguationData":[OSD([sQuery(id+"F2.wireOp",EDGE,"ed49934d-06d9-406b-9f25-b05f826b0471.4.0")])]})])],"derivedFrom":makeQuery(id+"F1.opRevolve","SWEPT_FACE",FACE,{"disambiguationData":[OSD([sQuery(id+"F0.wireOp",EDGE,"E24")])]})}),makeQuery(id+"F5.opExtrude","SWEPT_FACE",FACE,{"disambiguationData":[OSD([sQuery(id+"F4.wireOp",EDGE,"E35.4.0")])]})]});
            var Q13;
            Q13=makeQuery(id+"F5.boolean.opBoolean","INTERSECT",EDGE,{"derivedFrom":[makeQuery(id+"F3.boolean.opBoolean","SPLIT",FACE,{"disambiguationData":[TD([makeQuery(id+"F1.opRevolve","SWEPT_FACE",FACE,{"disambiguationData":[OSD([sQuery(id+"F0.wireOp",EDGE,"E11")])]}),makeQuery(id+"F1.opRevolve","SWEPT_FACE",FACE,{"disambiguationData":[OSD([sQuery(id+"F0.wireOp",EDGE,"E25")])]}),makeQuery(id+"F3.opExtrude","SWEPT_FACE",FACE,{"disambiguationData":[OSD([sQuery(id+"F2.wireOp",EDGE,"ed49934d-06d9-406b-9f25-b05f826b0471.3.0")])]}),makeQuery(id+"F3.opExtrude","SWEPT_FACE",FACE,{"disambiguationData":[OSD([sQuery(id+"F2.wireOp",EDGE,"ed49934d-06d9-406b-9f25-b05f826b0471.4.0")])]})])],"derivedFrom":makeQuery(id+"F1.opRevolve","SWEPT_FACE",FACE,{"disambiguationData":[OSD([sQuery(id+"F0.wireOp",EDGE,"E24")])]})}),makeQuery(id+"F5.opExtrude","SWEPT_FACE",FACE,{"disambiguationData":[OSD([sQuery(id+"F4.wireOp",EDGE,"E35.4.0")])]})]});
            var Q14;
            Q14=makeQuery(id+"F5.boolean.opBoolean","INTERSECT",EDGE,{"derivedFrom":[makeQuery(id+"F3.boolean.opBoolean","SPLIT",FACE,{"disambiguationData":[TD([makeQuery(id+"F1.opRevolve","SWEPT_FACE",FACE,{"disambiguationData":[OSD([sQuery(id+"F0.wireOp",EDGE,"E11")])]}),makeQuery(id+"F1.opRevolve","SWEPT_FACE",FACE,{"disambiguationData":[OSD([sQuery(id+"F0.wireOp",EDGE,"E25")])]}),makeQuery(id+"F3.opExtrude","SWEPT_FACE",FACE,{"disambiguationData":[OSD([sQuery(id+"F2.wireOp",EDGE,"ed49934d-06d9-406b-9f25-b05f826b0471.3.0")])]}),makeQuery(id+"F3.opExtrude","SWEPT_FACE",FACE,{"disambiguationData":[OSD([sQuery(id+"F2.wireOp",EDGE,"ed49934d-06d9-406b-9f25-b05f826b0471.4.0")])]})])],"derivedFrom":makeQuery(id+"F1.opRevolve","SWEPT_FACE",FACE,{"disambiguationData":[OSD([sQuery(id+"F0.wireOp",EDGE,"E24")])]})}),makeQuery(id+"F5.opExtrude","SWEPT_FACE",FACE,{"disambiguationData":[OSD([sQuery(id+"F4.wireOp",EDGE,"E35.3.0")])]})]});
            var Q15;
            Q15=makeQuery(id+"F5.boolean.opBoolean","INTERSECT",EDGE,{"derivedFrom":[makeQuery(id+"F3.boolean.opBoolean","SPLIT",FACE,{"disambiguationData":[TD([makeQuery(id+"F1.opRevolve","SWEPT_FACE",FACE,{"disambiguationData":[OSD([sQuery(id+"F0.wireOp",EDGE,"E11")])]}),makeQuery(id+"F1.opRevolve","SWEPT_FACE",FACE,{"disambiguationData":[OSD([sQuery(id+"F0.wireOp",EDGE,"E25")])]}),makeQuery(id+"F3.opExtrude","SWEPT_FACE",FACE,{"disambiguationData":[OSD([sQuery(id+"F2.wireOp",EDGE,"ed49934d-06d9-406b-9f25-b05f826b0471.2.0")])]}),makeQuery(id+"F3.opExtrude","SWEPT_FACE",FACE,{"disambiguationData":[OSD([sQuery(id+"F2.wireOp",EDGE,"ed49934d-06d9-406b-9f25-b05f826b0471.3.0")])]})])],"derivedFrom":makeQuery(id+"F1.opRevolve","SWEPT_FACE",FACE,{"disambiguationData":[OSD([sQuery(id+"F0.wireOp",EDGE,"E24")])]})}),makeQuery(id+"F5.opExtrude","SWEPT_FACE",FACE,{"disambiguationData":[OSD([sQuery(id+"F4.wireOp",EDGE,"E35.3.0")])]})]});
            var Q16;
            Q16=makeQuery(id+"F5.boolean.opBoolean","INTERSECT",EDGE,{"derivedFrom":[makeQuery(id+"F3.boolean.opBoolean","SPLIT",FACE,{"disambiguationData":[TD([makeQuery(id+"F1.opRevolve","SWEPT_FACE",FACE,{"disambiguationData":[OSD([sQuery(id+"F0.wireOp",EDGE,"E11")])]}),makeQuery(id+"F1.opRevolve","SWEPT_FACE",FACE,{"disambiguationData":[OSD([sQuery(id+"F0.wireOp",EDGE,"E25")])]}),makeQuery(id+"F3.opExtrude","SWEPT_FACE",FACE,{"disambiguationData":[OSD([sQuery(id+"F2.wireOp",EDGE,"ed49934d-06d9-406b-9f25-b05f826b0471.2.0")])]}),makeQuery(id+"F3.opExtrude","SWEPT_FACE",FACE,{"disambiguationData":[OSD([sQuery(id+"F2.wireOp",EDGE,"ed49934d-06d9-406b-9f25-b05f826b0471.3.0")])]})])],"derivedFrom":makeQuery(id+"F1.opRevolve","SWEPT_FACE",FACE,{"disambiguationData":[OSD([sQuery(id+"F0.wireOp",EDGE,"E24")])]})}),makeQuery(id+"F5.opExtrude","SWEPT_FACE",FACE,{"disambiguationData":[OSD([sQuery(id+"F4.wireOp",EDGE,"E35.2.0")])]})]});
            var Q17;
            Q17=makeQuery(id+"F5.boolean.opBoolean","INTERSECT",EDGE,{"derivedFrom":[makeQuery(id+"F3.boolean.opBoolean","SPLIT",FACE,{"disambiguationData":[TD([makeQuery(id+"F1.opRevolve","SWEPT_FACE",FACE,{"disambiguationData":[OSD([sQuery(id+"F0.wireOp",EDGE,"E11")])]}),makeQuery(id+"F1.opRevolve","SWEPT_FACE",FACE,{"disambiguationData":[OSD([sQuery(id+"F0.wireOp",EDGE,"E25")])]}),makeQuery(id+"F3.opExtrude","SWEPT_FACE",FACE,{"disambiguationData":[OSD([sQuery(id+"F2.wireOp",EDGE,"ed49934d-06d9-406b-9f25-b05f826b0471.1.0")])]}),makeQuery(id+"F3.opExtrude","SWEPT_FACE",FACE,{"disambiguationData":[OSD([sQuery(id+"F2.wireOp",EDGE,"ed49934d-06d9-406b-9f25-b05f826b0471.2.0")])]})])],"derivedFrom":makeQuery(id+"F1.opRevolve","SWEPT_FACE",FACE,{"disambiguationData":[OSD([sQuery(id+"F0.wireOp",EDGE,"E24")])]})}),makeQuery(id+"F5.opExtrude","SWEPT_FACE",FACE,{"disambiguationData":[OSD([sQuery(id+"F4.wireOp",EDGE,"E35.2.0")])]})]});
            var Q18;
            Q18=makeQuery(id+"F5.boolean.opBoolean","INTERSECT",EDGE,{"derivedFrom":[makeQuery(id+"F3.boolean.opBoolean","SPLIT",FACE,{"disambiguationData":[TD([makeQuery(id+"F1.opRevolve","SWEPT_FACE",FACE,{"disambiguationData":[OSD([sQuery(id+"F0.wireOp",EDGE,"E11")])]}),makeQuery(id+"F1.opRevolve","SWEPT_FACE",FACE,{"disambiguationData":[OSD([sQuery(id+"F0.wireOp",EDGE,"E25")])]}),makeQuery(id+"F3.opExtrude","SWEPT_FACE",FACE,{"disambiguationData":[OSD([sQuery(id+"F2.wireOp",EDGE,"ed49934d-06d9-406b-9f25-b05f826b0471.1.0")])]}),makeQuery(id+"F3.opExtrude","SWEPT_FACE",FACE,{"disambiguationData":[OSD([sQuery(id+"F2.wireOp",EDGE,"ed49934d-06d9-406b-9f25-b05f826b0471.2.0")])]})])],"derivedFrom":makeQuery(id+"F1.opRevolve","SWEPT_FACE",FACE,{"disambiguationData":[OSD([sQuery(id+"F0.wireOp",EDGE,"E24")])]})}),makeQuery(id+"F5.opExtrude","SWEPT_FACE",FACE,{"disambiguationData":[OSD([sQuery(id+"F4.wireOp",EDGE,"E35.1.0")])]})]});
            var Q19;
            Q19=makeQuery(id+"F5.boolean.opBoolean","INTERSECT",EDGE,{"derivedFrom":[makeQuery(id+"F3.boolean.opBoolean","SPLIT",FACE,{"disambiguationData":[TD([makeQuery(id+"F1.opRevolve","SWEPT_FACE",FACE,{"disambiguationData":[OSD([sQuery(id+"F0.wireOp",EDGE,"E11")])]}),makeQuery(id+"F1.opRevolve","SWEPT_FACE",FACE,{"disambiguationData":[OSD([sQuery(id+"F0.wireOp",EDGE,"E25")])]}),makeQuery(id+"F3.opExtrude","SWEPT_FACE",FACE,{"disambiguationData":[OSD([sQuery(id+"F2.wireOp",EDGE,"isoNOGXv-9rzR-vXjO-d8jj-fEhT8795Os4k")])]}),makeQuery(id+"F3.opExtrude","SWEPT_FACE",FACE,{"disambiguationData":[OSD([sQuery(id+"F2.wireOp",EDGE,"ed49934d-06d9-406b-9f25-b05f826b0471.1.0")])]})])],"derivedFrom":makeQuery(id+"F1.opRevolve","SWEPT_FACE",FACE,{"disambiguationData":[OSD([sQuery(id+"F0.wireOp",EDGE,"E24")])]})}),makeQuery(id+"F5.opExtrude","SWEPT_FACE",FACE,{"disambiguationData":[OSD([sQuery(id+"F4.wireOp",EDGE,"E35.1.0")])]})]});
            chamfer(context, id + "F15", {"entities" : qUnion([Q0, Q1, Q2, Q3, Q4, Q5, Q6, Q7, Q8, Q9, Q10, Q11, Q12, Q13, Q14, Q15, Q16, Q17, Q18, Q19]), "width" : 1 * mm, "tangentPropagation" : true});
        }
        {
            var Q0;
            Q0=makeQuery(id+"F5.boolean.opBoolean","MERGE",FACE,{"derivedFrom":[makeQuery(id+"F1.opRevolve","SWEPT_FACE",FACE,{"disambiguationData":[OSD([sQuery(id+"F0.wireOp",EDGE,"E7")])]}),makeQuery(id+"F5.opExtrude","CAP_FACE",FACE,{"disambiguationData":[OSD([sQuery(id+"F4.wireOp",EDGE,"E34")])],"isStart":false}),makeQuery(id+"F5.opExtrude","CAP_FACE",FACE,{"disambiguationData":[OSD([sQuery(id+"F4.wireOp",EDGE,"E35.1.0")])],"isStart":false}),makeQuery(id+"F5.opExtrude","CAP_FACE",FACE,{"disambiguationData":[OSD([sQuery(id+"F4.wireOp",EDGE,"E35.2.0")])],"isStart":false}),makeQuery(id+"F5.opExtrude","CAP_FACE",FACE,{"disambiguationData":[OSD([sQuery(id+"F4.wireOp",EDGE,"E35.3.0")])],"isStart":false}),makeQuery(id+"F5.opExtrude","CAP_FACE",FACE,{"disambiguationData":[OSD([sQuery(id+"F4.wireOp",EDGE,"E35.4.0")])],"isStart":false})]});
            var sketch = newSketch(context, id + "F16", { "sketchPlane" : qUnion([Q0])});
            skPoint(sketch, "E52", {"position": v(-72.5, 0) * mm});
            skPoint(sketch, "E53", {"position": v(72.5, 0) * mm});
            skCircle(sketch, "E54", {"center": v(-72.5, 0) * mm, "radius": 4 * mm});
            skCircle(sketch, "E55", {"center": v(72.5, 0) * mm, "radius": 4 * mm});
            skSolve(sketch);
        }
        {
            var Q0;
            Q0=qSketchRegion(id+"F16",true);
            extrude(context, id + "F17", {"entities" : qUnion([Q0]), "operationType" : NewBodyOperationType.REMOVE, "oppositeDirection" : true, "depth" : 10.22 * mm});
        }
        {
            var Q0;
            Q0=makeQuery(id+"F1.opRevolve","SWEPT_EDGE",EDGE,{"disambiguationData":[OSD([sQuery(id+"F0.wireOp",EDGE,"E13"),sQuery(id+"F0.wireOp",EDGE,"E16")])]});
            var Q1;
            Q1=makeQuery(id+"F1.opRevolve","SWEPT_EDGE",EDGE,{"disambiguationData":[OSD([sQuery(id+"F0.wireOp",EDGE,"E15"),sQuery(id+"F0.wireOp",EDGE,"E16")])]});
            var Q2;
            Q2=makeQuery(id+"F1.opRevolve","SWEPT_EDGE",EDGE,{"disambiguationData":[OSD([sQuery(id+"F0.wireOp",EDGE,"E5"),sQuery(id+"F0.wireOp",EDGE,"E7")])]});
            var Q3;
            Q3=makeQuery(id+"F1.opRevolve","SWEPT_EDGE",EDGE,{"disambiguationData":[OSD([sQuery(id+"F0.wireOp",EDGE,"E4"),sQuery(id+"F0.wireOp",EDGE,"E5")])]});
            chamfer(context, id + "F18", {"entities" : qUnion([Q0, Q1, Q2, Q3]), "width" : .5 * mm, "tangentPropagation" : true});
        }
    });
